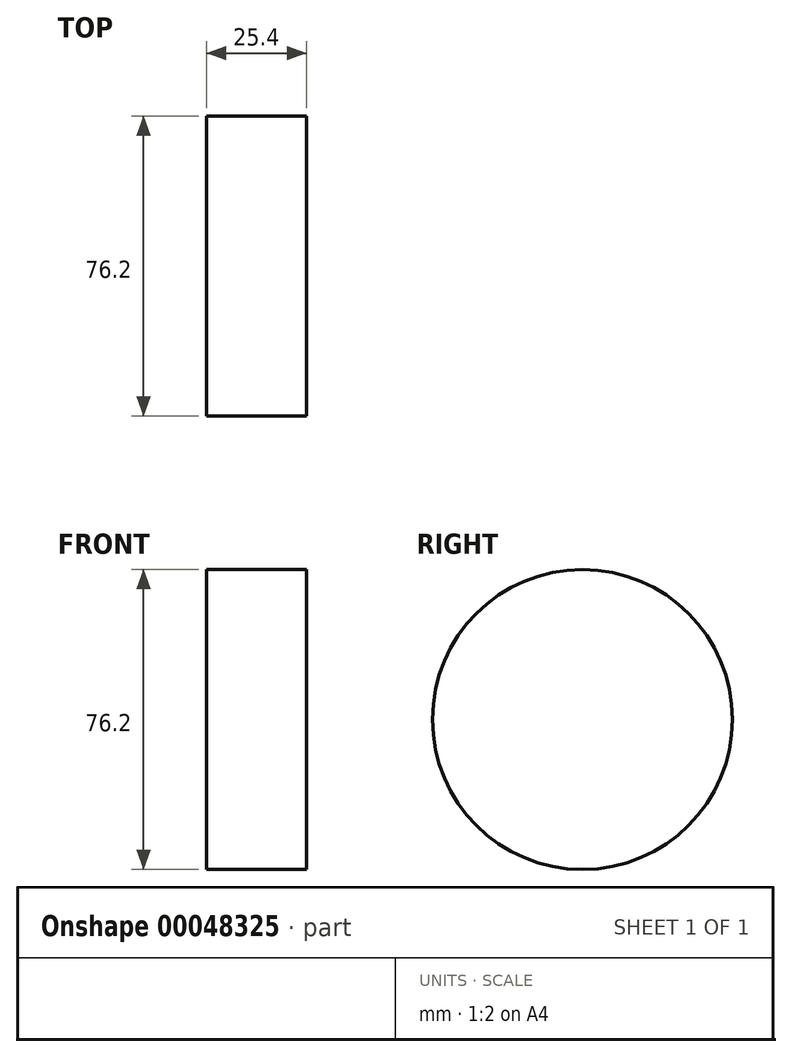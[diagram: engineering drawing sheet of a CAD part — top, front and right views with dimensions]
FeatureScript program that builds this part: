
annotation { "Feature Type Name" : "Feature", "Feature Type Description" : "" }
export const myFeature = defineFeature(function(context is Context, id is Id, definition is map)
    precondition{}
    {
        {
            var Q0;
            Q0=qCreatedBy(makeId("Right.planeOp"),FACE);
            var sketch = newSketch(context, id + "F0", { "sketchPlane" : qUnion([Q0])});
            skCircle(sketch, "E0", {"center": v(0, 0) * mm, "radius": 38.1 * mm});
            skSolve(sketch);
        }
        {
            var Q0;
            Q0 = qSketchRegion(id + "F0", true);
            extrude(context, id + "F1", {"entities" : qUnion([Q0]), "depth" : 25.4 * mm});
        }
    });
